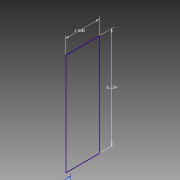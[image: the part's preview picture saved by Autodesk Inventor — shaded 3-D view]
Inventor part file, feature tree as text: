
AUTODESK INVENTOR PART (.ipt)
format: ipt  version: 2015 (Build 190159000, 159)  size: 60,416 bytes
history: native  units: in
note: dims shown in document units (in); Inventor stores cm internally (conversion verified against a paired STEP export)
features: sketch x1
ambient origin geometry x8: Origin, YZ Plane, XZ Plane, XY Plane, X Axis, Y Axis, Z Axis, Center Point
feature tree (1):
  sketch  "Sketch1"  dims[d0=6.124in d1=2.0in]
